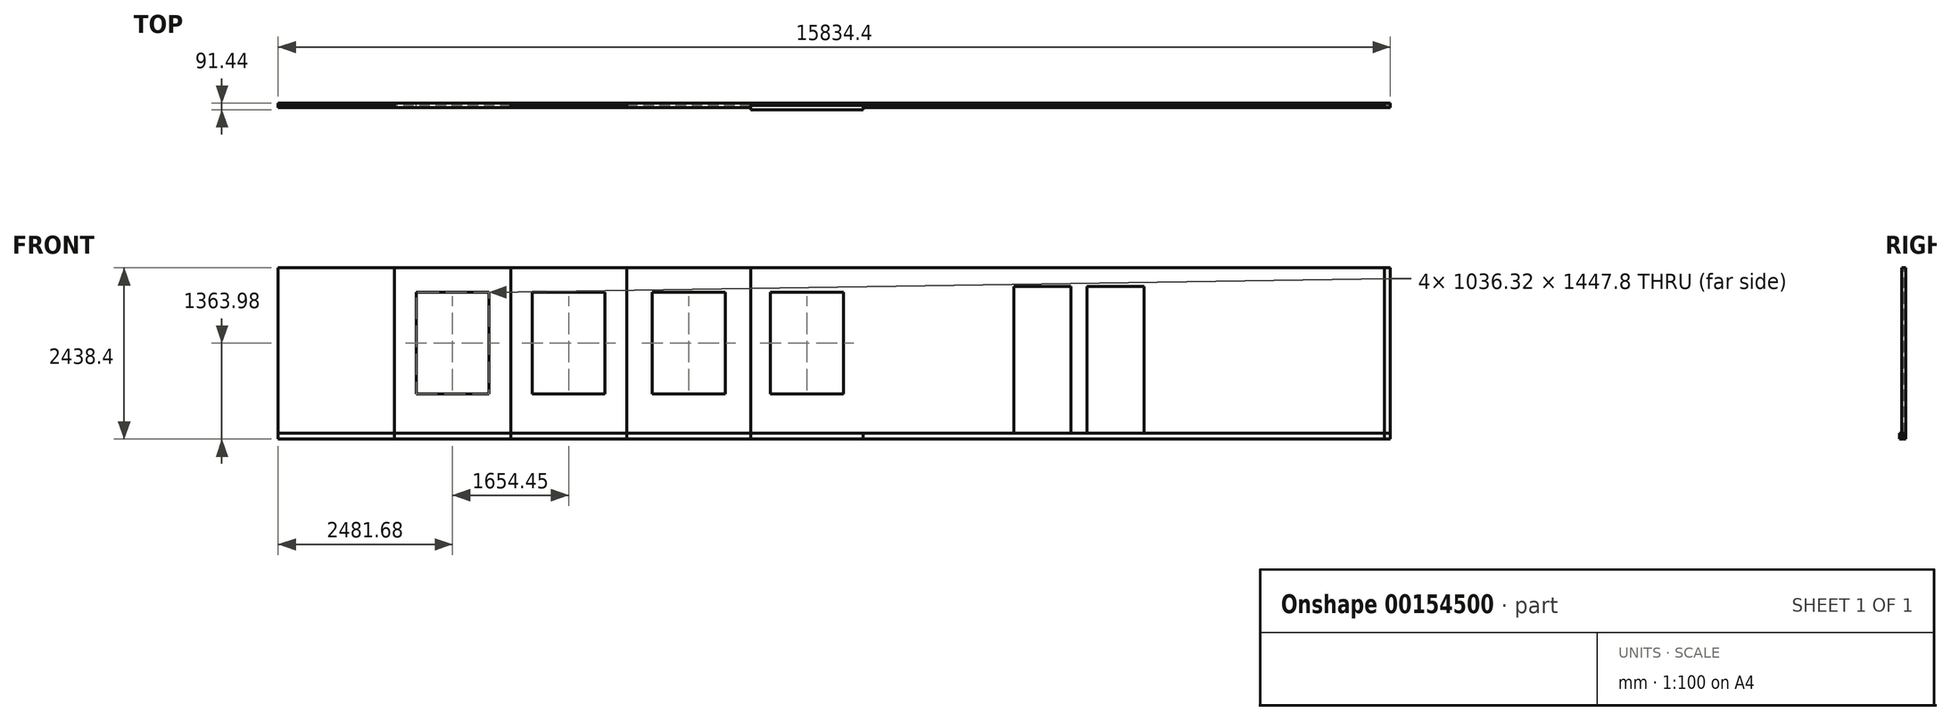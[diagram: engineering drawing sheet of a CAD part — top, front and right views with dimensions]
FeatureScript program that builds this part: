
annotation { "Feature Type Name" : "Feature", "Feature Type Description" : "" }
export const myFeature = defineFeature(function(context is Context, id is Id, definition is map)
    precondition{}
    {
        {
            var Q0;
            Q0=qCreatedBy(makeId("Front.planeOp"),FACE);
            var sketch = newSketch(context, id + "F0", { "sketchPlane" : qUnion([Q0])});
            skLineSegment(sketch, "E0.bottom", {"start": v(0, 0) * mm, "end": v(1654.45, 0) * mm});
            skLineSegment(sketch, "E0.top", {"start": v(0, 2438.4) * mm, "end": v(1654.45, 2438.4) * mm});
            skLineSegment(sketch, "E0.left", {"start": v(0, 0) * mm, "end": v(0, 2438.4) * mm});
            skLineSegment(sketch, "E0.right", {"start": v(1654.45, 0) * mm, "end": v(1654.45, 2438.4) * mm});
            skLineSegment(sketch, "E1", {"start": v(1654.45, 2438.4) * mm, "end": v(3308.9, 2438.4) * mm});
            skLineSegment(sketch, "E2", {"start": v(3308.9, 2438.4) * mm, "end": v(3308.9, 0) * mm});
            skLineSegment(sketch, "E3", {"start": v(3308.9, 0) * mm, "end": v(1654.45, 0) * mm});
            skLineSegment(sketch, "E4", {"start": v(3308.9, 2438.4) * mm, "end": v(4963.36, 2438.4) * mm});
            skLineSegment(sketch, "E5", {"start": v(4963.36, 2438.4) * mm, "end": v(4963.36, 0) * mm});
            skLineSegment(sketch, "E6", {"start": v(4963.36, 0) * mm, "end": v(3308.9, 0) * mm});
            skLineSegment(sketch, "E7", {"start": v(4963.36, 2438.4) * mm, "end": v(6727.85, 2438.4) * mm});
            skLineSegment(sketch, "E8", {"start": v(6727.85, 2438.4) * mm, "end": v(6727.85, 0) * mm});
            skLineSegment(sketch, "E9", {"start": v(6727.85, 0) * mm, "end": v(4963.36, 0) * mm});
            skLineSegment(sketch, "E10", {"start": v(6727.85, 2438.4) * mm, "end": v(8327.44, 2438.4) * mm});
            skLineSegment(sketch, "E11", {"start": v(8327.44, 2438.4) * mm, "end": v(8327.44, 0) * mm});
            skLineSegment(sketch, "E12", {"start": v(8327.44, 0) * mm, "end": v(6727.85, 0) * mm});
            skLineSegment(sketch, "E13", {"start": v(8327.44, 2438.4) * mm, "end": v(15834.36, 2438.4) * mm});
            skLineSegment(sketch, "E14", {"start": v(15834.36, 2438.4) * mm, "end": v(15834.36, 0) * mm});
            skLineSegment(sketch, "E15", {"start": v(15834.36, 0) * mm, "end": v(8327.44, 0) * mm});
            skLineSegment(sketch, "E16", {"start": v(0, 82.6) * mm, "end": v(15834.36, 82.6) * mm});
            skLineSegment(sketch, "E17", {"start": v(15751.76, 2438.4) * mm, "end": v(15751.76, 0) * mm});
            skLineSegment(sketch, "E18.bottom", {"start": v(1963.52, 2087.88) * mm, "end": v(2999.84, 2087.88) * mm});
            skLineSegment(sketch, "E18.top", {"start": v(1963.52, 640.08) * mm, "end": v(2999.84, 640.08) * mm});
            skLineSegment(sketch, "E18.left", {"start": v(1963.52, 2087.88) * mm, "end": v(1963.52, 640.08) * mm});
            skLineSegment(sketch, "E18.right", {"start": v(2999.84, 2087.88) * mm, "end": v(2999.84, 640.08) * mm});
            skPoint(sketch, "E19.oppositeSnap0", {"position": v(2481.68, 640.08) * mm});
            skLineSegment(sketch, "E19.bottom", {"start": v(3617.98, 2087.88) * mm, "end": v(4654.3, 2087.88) * mm});
            skLineSegment(sketch, "E19.top", {"start": v(3617.98, 640.08) * mm, "end": v(4654.3, 640.08) * mm});
            skLineSegment(sketch, "E19.left", {"start": v(3617.98, 2087.88) * mm, "end": v(3617.98, 640.08) * mm});
            skLineSegment(sketch, "E19.right", {"start": v(4654.3, 2087.88) * mm, "end": v(4654.3, 640.08) * mm});
            skPoint(sketch, "E20.firstSnap0", {"position": v(4136.14, 2087.88) * mm});
            skLineSegment(sketch, "E20.bottom", {"start": v(5327.45, 2087.88) * mm, "end": v(6363.77, 2087.88) * mm});
            skLineSegment(sketch, "E20.top", {"start": v(5327.45, 640.08) * mm, "end": v(6363.77, 640.08) * mm});
            skLineSegment(sketch, "E20.left", {"start": v(5327.45, 2087.88) * mm, "end": v(5327.45, 640.08) * mm});
            skLineSegment(sketch, "E20.right", {"start": v(6363.77, 2087.88) * mm, "end": v(6363.77, 640.08) * mm});
            skLineSegment(sketch, "E21.bottom", {"start": v(7009.49, 2087.88) * mm, "end": v(8045.8, 2087.88) * mm});
            skLineSegment(sketch, "E21.top", {"start": v(7009.49, 640.08) * mm, "end": v(8045.8, 640.08) * mm});
            skLineSegment(sketch, "E21.left", {"start": v(7009.49, 2087.88) * mm, "end": v(7009.49, 640.08) * mm});
            skLineSegment(sketch, "E21.right", {"start": v(8045.8, 2087.88) * mm, "end": v(8045.8, 640.08) * mm});
            skLineSegment(sketch, "E22", {"start": v(10473.84, 82.6) * mm, "end": v(10473.84, 2170.48) * mm});
            skLineSegment(sketch, "E23", {"start": v(10473.84, 2170.48) * mm, "end": v(11286.74, 2170.48) * mm});
            skLineSegment(sketch, "E24", {"start": v(11286.74, 2170.48) * mm, "end": v(11286.74, 82.6) * mm});
            skLineSegment(sketch, "E25", {"start": v(11362.94, 2438.4) * mm, "end": v(11362.94, 0) * mm, "construction": true});
            skLineSegment(sketch, "E26", {"start": v(11515.34, 82.6) * mm, "end": v(11515.34, 2170.48) * mm});
            skLineSegment(sketch, "E27", {"start": v(11515.34, 2170.48) * mm, "end": v(12328.25, 2170.48) * mm});
            skLineSegment(sketch, "E28", {"start": v(12328.25, 2170.48) * mm, "end": v(12328.25, 82.6) * mm});
            skLineSegment(sketch, "E29", {"start": v(7527.65, 2087.88) * mm, "end": v(7527.65, 2438.4) * mm, "construction": true});
            skLineSegment(sketch, "E30", {"start": v(5845.6, 2087.88) * mm, "end": v(5845.6, 2438.4) * mm, "construction": true});
            skLineSegment(sketch, "E31", {"start": v(4136.14, 2087.88) * mm, "end": v(4136.14, 2438.4) * mm, "construction": true});
            skLineSegment(sketch, "E32", {"start": v(2481.68, 2087.88) * mm, "end": v(2481.68, 2438.4) * mm, "construction": true});
            skSolve(sketch);
        }
        {
            var Q0;
            {var subQ0=sQuery(id+"F0.wireOp",EDGE,"E0.top");Q0=makeQuery(id+"F0.imprint","IMPRINT",FACE,{"disambiguationData":[TD([[makeQuery(id+"F0.imprint","IMPRINT",EDGE,{"derivedFrom":subQ0}),-1.0]])]});}
            var Q1;
            {var subQ0=sQuery(id+"F0.wireOp",EDGE,"E3");Q1=makeQuery(id+"F0.imprint","IMPRINT",FACE,{"disambiguationData":[TD([[makeQuery(id+"F0.imprint","IMPRINT",EDGE,{"derivedFrom":subQ0}),-1.0]])]});}
            var Q2;
            {var subQ5=sQuery(id+"F0.wireOp",EDGE,"E4");Q2=makeQuery(id+"F0.imprint","IMPRINT",FACE,{"disambiguationData":[TD([[makeQuery(id+"F0.imprint","IMPRINT",EDGE,{"derivedFrom":subQ5}),-1.0]])]});}
            var Q3;
            {var subQ0=sQuery(id+"F0.wireOp",EDGE,"E9");Q3=makeQuery(id+"F0.imprint","IMPRINT",FACE,{"disambiguationData":[TD([[makeQuery(id+"F0.imprint","IMPRINT",EDGE,{"derivedFrom":subQ0}),-1.0]])]});}
            var Q4;
            {var subQ1=sQuery(id+"F0.wireOp",EDGE,"E10");Q4=makeQuery(id+"F0.imprint","IMPRINT",FACE,{"disambiguationData":[TD([[makeQuery(id+"F0.imprint","IMPRINT",EDGE,{"derivedFrom":subQ1}),-1.0]])]});}
            var Q5;
            {var subQ6=sQuery(id+"F0.wireOp",EDGE,"E22");Q5=makeQuery(id+"F0.imprint","IMPRINT",FACE,{"disambiguationData":[TD([[makeQuery(id+"F0.imprint","IMPRINT",EDGE,{"derivedFrom":subQ6}),1.0]])]});}
            var Q6;
            {var subQ0=sQuery(id+"F0.wireOp",EDGE,"E15");var subQ1=sQuery(id+"F0.wireOp",EDGE,"E14");var subQ2=makeQuery(id+"F0.imprint","INTERSECT",VERTEX,{"derivedFrom":[subQ1,subQ0]});Q6=makeQuery(id+"F0.imprint","IMPRINT",FACE,{"disambiguationData":[TD([[makeQuery(id+"F0.imprint","IMPRINT",EDGE,{"disambiguationData":[TD([[subQ2,1.0]])],"derivedFrom":subQ1}),-1.0]])]});}
            extrude(context, id + "F1", {"entities" : qUnion([Q0, Q1, Q2, Q3, Q4, Q5, Q6]), "depth" : 30.48 * mm});
        }
        {
            var Q0;
            {var subQ0=sQuery(id+"F0.wireOp",EDGE,"E16");var subQ1=makeQuery(id+"F0.imprint","INTERSECT",VERTEX,{"derivedFrom":[subQ0,sQuery(id+"F0.wireOp",EDGE,"E22")]});Q0=makeQuery(id+"F0.imprint","IMPRINT",FACE,{"disambiguationData":[TD([[makeQuery(id+"F0.imprint","IMPRINT",EDGE,{"disambiguationData":[TD([[subQ1,1.0]])],"derivedFrom":subQ0}),-1.0]])]});}
            var Q1;
            {var subQ0=sQuery(id+"F0.wireOp",EDGE,"E14");var subQ1=sQuery(id+"F0.wireOp",EDGE,"E13");var subQ2=makeQuery(id+"F0.imprint","INTERSECT",VERTEX,{"derivedFrom":[subQ1,subQ0]});Q1=makeQuery(id+"F0.imprint","IMPRINT",FACE,{"disambiguationData":[TD([[makeQuery(id+"F0.imprint","IMPRINT",EDGE,{"disambiguationData":[TD([[subQ2,1.0]])],"derivedFrom":subQ1}),-1.0]])]});}
            var Q2;
            {var subQ5=sQuery(id+"F0.wireOp",EDGE,"E7");Q2=makeQuery(id+"F0.imprint","IMPRINT",FACE,{"disambiguationData":[TD([[makeQuery(id+"F0.imprint","IMPRINT",EDGE,{"derivedFrom":subQ5}),-1.0]])]});}
            var Q3;
            {var subQ5=sQuery(id+"F0.wireOp",EDGE,"E1");Q3=makeQuery(id+"F0.imprint","IMPRINT",FACE,{"disambiguationData":[TD([[makeQuery(id+"F0.imprint","IMPRINT",EDGE,{"derivedFrom":subQ5}),-1.0]])]});}
            var Q4;
            {var subQ0=sQuery(id+"F0.wireOp",EDGE,"E6");Q4=makeQuery(id+"F0.imprint","IMPRINT",FACE,{"disambiguationData":[TD([[makeQuery(id+"F0.imprint","IMPRINT",EDGE,{"derivedFrom":subQ0}),-1.0]])]});}
            var Q5;
            {var subQ0=sQuery(id+"F0.wireOp",EDGE,"E0.bottom");Q5=makeQuery(id+"F0.imprint","IMPRINT",FACE,{"disambiguationData":[TD([[makeQuery(id+"F0.imprint","IMPRINT",EDGE,{"derivedFrom":subQ0}),1.0]])]});}
            extrude(context, id + "F2", {"entities" : qUnion([Q0, Q1, Q2, Q3, Q4, Q5]), "depth" : 60.96 * mm});
        }
        {
            var Q0;
            {var subQ0=sQuery(id+"F0.wireOp",EDGE,"E12");Q0=makeQuery(id+"F0.imprint","IMPRINT",FACE,{"disambiguationData":[TD([[makeQuery(id+"F0.imprint","IMPRINT",EDGE,{"derivedFrom":subQ0}),-1.0]])]});}
            extrude(context, id + "F3", {"entities" : qUnion([Q0]), "depth" : 91.44 * mm});
        }
    });
